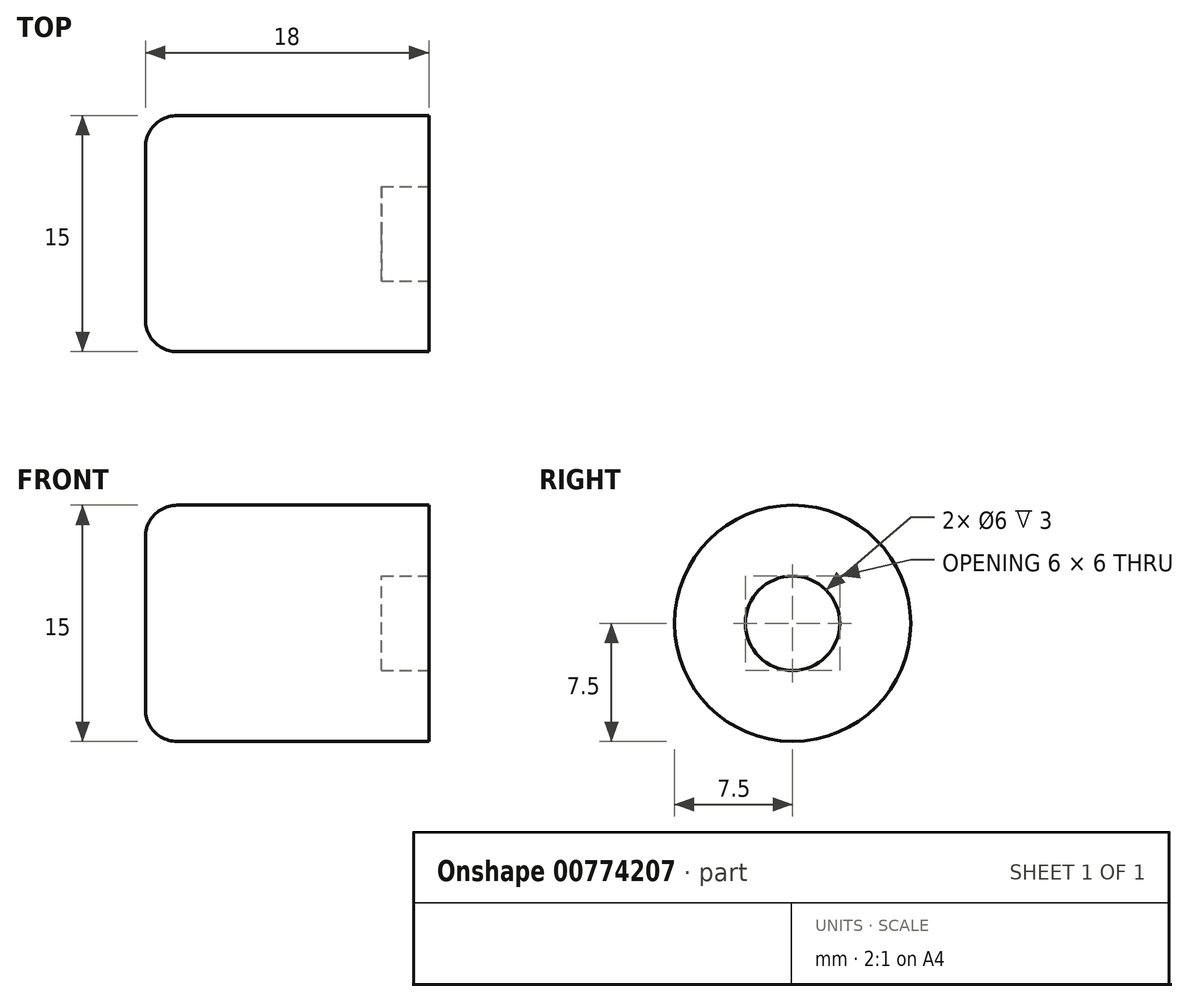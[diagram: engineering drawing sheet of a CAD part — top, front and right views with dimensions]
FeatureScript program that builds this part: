
annotation { "Feature Type Name" : "Feature", "Feature Type Description" : "" }
export const myFeature = defineFeature(function(context is Context, id is Id, definition is map)
    precondition{}
    {
        {
            var Q0;
            Q0=qCreatedBy(makeId("Front.planeOp"),FACE);
            var sketch = newSketch(context, id + "F0", { "sketchPlane" : qUnion([Q0])});
            skLineSegment(sketch, "E0.bottom", {"start": v(-15, 10) * mm, "end": v(15, 10) * mm});
            skLineSegment(sketch, "E0.top", {"start": v(-15, -10) * mm, "end": v(15, -10) * mm});
            skLineSegment(sketch, "E0.left", {"start": v(-15, 10) * mm, "end": v(-15, -10) * mm});
            skLineSegment(sketch, "E0.right", {"start": v(15, 10) * mm, "end": v(15, -10) * mm});
            skLineSegment(sketch, "E1", {"start": v(-17, 12) * mm, "end": v(-17, -12) * mm});
            skLineSegment(sketch, "E2", {"start": v(-17, -12) * mm, "end": v(17, -12) * mm});
            skLineSegment(sketch, "E3", {"start": v(17, -12) * mm, "end": v(17, 12) * mm});
            skLineSegment(sketch, "E4", {"start": v(17, 12) * mm, "end": v(-17, 12) * mm});
            skSolve(sketch);
        }
        {
            var Q0;
            Q0=makeQuery(id+"F0.imprint","IMPRINT",FACE,{"disambiguationData":[TD([[makeQuery(id+"F0.imprint","IMPRINT",EDGE,{"derivedFrom":sQuery(id+"F0.wireOp",EDGE,"E0.bottom")}),1.0]])]});
            extrude(context, id + "F1", {"entities" : qUnion([Q0]), "depth" : 20 * mm, "offsetDistance" : 25 * mm});
        }
        {
            var Q0;
            Q0=makeQuery(id+"F1.opExtrude","SWEPT_FACE",FACE,{"disambiguationData":[OSD([sQuery(id+"F0.wireOp",EDGE,"E4")])]});
            var sketch = newSketch(context, id + "F2", { "sketchPlane" : qUnion([Q0])});
            skCircle(sketch, "E5", {"center": v(6, -10) * mm, "radius": 6.5 * mm});
            skSolve(sketch);
        }
        {
            var Q0;
            Q0 = qSketchRegion(id + "F2", true);
            extrude(context, id + "F3", {"entities" : qUnion([Q0]), "operationType" : NewBodyOperationType.REMOVE, "oppositeDirection" : true, "depth" : 11.7 * mm, "offsetDistance" : 25 * mm});
        }
        {
            var Q0;
            Q0=makeQuery(id+"F1.opExtrude","SWEPT_FACE",FACE,{"disambiguationData":[OSD([sQuery(id+"F0.wireOp",EDGE,"E2")])]});
            var sketch = newSketch(context, id + "F4", { "sketchPlane" : qUnion([Q0])});
            skCircle(sketch, "E6", {"center": v(-5, 10) * mm, "radius": 7.5 * mm});
            skSolve(sketch);
        }
        {
            var Q0;
            Q0 = qSketchRegion(id + "F4", true);
            extrude(context, id + "F5", {"entities" : qUnion([Q0]), "operationType" : NewBodyOperationType.REMOVE, "oppositeDirection" : true, "depth" : 8.3 * mm, "offsetDistance" : 25 * mm});
        }
        {
            var Q0;
            Q0=makeQuery(id+"F1.opExtrude","SWEPT_FACE",FACE,{"disambiguationData":[OSD([sQuery(id+"F0.wireOp",EDGE,"E1")])]});
            var sketch = newSketch(context, id + "F6", { "sketchPlane" : qUnion([Q0])});
            skCircle(sketch, "E7", {"center": v(10, 0) * mm, "radius": 7.5 * mm});
            skSolve(sketch);
        }
        {
            var Q0;
            Q0 = qSketchRegion(id + "F6", true);
            extrude(context, id + "F7", {"entities" : qUnion([Q0]), "operationType" : NewBodyOperationType.ADD, "depth" : 18 * mm, "offsetDistance" : 25 * mm});
        }
        {
            var Q0;
            Q0=makeQuery(id+"F1.opExtrude","SWEPT_EDGE",EDGE,{"disambiguationData":[OSD([sQuery(id+"F0.wireOp",EDGE,"E1"),sQuery(id+"F0.wireOp",EDGE,"E4")])]});
            var Q1;
            Q1=makeQuery(id+"F1.opExtrude","SWEPT_EDGE",EDGE,{"disambiguationData":[OSD([sQuery(id+"F0.wireOp",EDGE,"E1"),sQuery(id+"F0.wireOp",EDGE,"E2")])]});
            var Q2;
            Q2=makeQuery(id+"F7.opExtrude","CAP_EDGE",EDGE,{"disambiguationData":[OSD([sQuery(id+"F6.wireOp",EDGE,"E7")])],"isStart":false});
            fillet(context, id + "F8", {"entities" : qUnion([Q0, Q1, Q2]), "radius" : 2 * mm, "tangentPropagation" : true, "allowEdgeOverflow" : false});
        }
        {
            var Q0;
            Q0=makeQuery(id+"F3.boolean.opBoolean","INTERSECT",EDGE,{"derivedFrom":[makeQuery(id+"F1.opExtrude","SWEPT_FACE",FACE,{"disambiguationData":[OSD([sQuery(id+"F0.wireOp",EDGE,"E0.bottom")])]}),makeQuery(id+"F3.opExtrude","SWEPT_FACE",FACE,{"disambiguationData":[OSD([sQuery(id+"F2.wireOp",EDGE,"E5")])]})]});
            var Q1;
            Q1=makeQuery(id+"F3.boolean.opBoolean","COPY",EDGE,{"derivedFrom":makeQuery(id+"F3.opExtrude","CAP_EDGE",EDGE,{"disambiguationData":[OSD([sQuery(id+"F2.wireOp",EDGE,"E5")])],"isStart":true})});
            var Q2;
            Q2=makeQuery(id+"F5.boolean.opBoolean","INTERSECT",EDGE,{"derivedFrom":[makeQuery(id+"F1.opExtrude","SWEPT_FACE",FACE,{"disambiguationData":[OSD([sQuery(id+"F0.wireOp",EDGE,"E0.top")])]}),makeQuery(id+"F5.opExtrude","SWEPT_FACE",FACE,{"disambiguationData":[OSD([sQuery(id+"F4.wireOp",EDGE,"E6")])]})]});
            var Q3;
            Q3=makeQuery(id+"F5.boolean.opBoolean","COPY",EDGE,{"derivedFrom":makeQuery(id+"F5.opExtrude","CAP_EDGE",EDGE,{"disambiguationData":[OSD([sQuery(id+"F4.wireOp",EDGE,"E6")])],"isStart":true})});
            fillet(context, id + "F9", {"entities" : qUnion([Q0, Q1, Q2, Q3]), "radius" : 1 * mm, "tangentPropagation" : true, "allowEdgeOverflow" : false});
        }
        {
            var Q0;
            Q0=makeQuery(id+"F1.opExtrude","CAP_FACE",FACE,{"disambiguationData":[OSD([sQuery(id+"F0.wireOp",EDGE,"E0.bottom"),sQuery(id+"F0.wireOp",EDGE,"E0.top"),sQuery(id+"F0.wireOp",EDGE,"E0.left"),sQuery(id+"F0.wireOp",EDGE,"E0.right"),sQuery(id+"F0.wireOp",EDGE,"E1"),sQuery(id+"F0.wireOp",EDGE,"E2"),sQuery(id+"F0.wireOp",EDGE,"E3"),sQuery(id+"F0.wireOp",EDGE,"E4")])],"isStart":false});
            var sketch = newSketch(context, id + "F10", { "sketchPlane" : qUnion([Q0])});
            skLineSegment(sketch, "E8.bottom", {"start": v(17, -10) * mm, "end": v(15, -10) * mm});
            skLineSegment(sketch, "E8.top", {"start": v(17, 10) * mm, "end": v(15, 10) * mm});
            skLineSegment(sketch, "E8.left", {"start": v(17, -10) * mm, "end": v(17, 10) * mm});
            skLineSegment(sketch, "E8.right", {"start": v(15, -10) * mm, "end": v(15, 10) * mm});
            skSolve(sketch);
        }
        {
            var Q0;
            Q0 = qSketchRegion(id + "F10", true);
            extrude(context, id + "F11", {"entities" : qUnion([Q0]), "operationType" : NewBodyOperationType.REMOVE, "oppositeDirection" : true, "depth" : 25 * mm, "offsetDistance" : 25 * mm});
        }
        {
            var Q0;
            Q0=qCreatedBy(makeId("Right.planeOp"),FACE);
            var sketch = newSketch(context, id + "F12", { "sketchPlane" : qUnion([Q0])});
            skLineSegment(sketch, "E9.bottom", {"start": v(-20, 12) * mm, "end": v(0, 12) * mm, "construction": true});
            skLineSegment(sketch, "E9.top", {"start": v(-20, -12) * mm, "end": v(0, -12) * mm, "construction": true});
            skLineSegment(sketch, "E9.left", {"start": v(-20, 12) * mm, "end": v(-20, -12) * mm, "construction": true});
            skLineSegment(sketch, "E9.right", {"start": v(0, 12) * mm, "end": v(0, -12) * mm, "construction": true});
            skArc(sketch, "E10", {"start": v(-20, 12) * mm, "mid": v(-21, 11) * mm, "end": v(-20, 10) * mm});
            skArc(sketch, "E11", {"start": v(-20, -10) * mm, "mid": v(-21, -11) * mm, "end": v(-20, -12) * mm});
            skArc(sketch, "E12", {"start": v(0, -12) * mm, "mid": v(1, -11) * mm, "end": v(0, -10) * mm});
            skArc(sketch, "E13", {"start": v(0, 10) * mm, "mid": v(1, 11) * mm, "end": v(0, 12) * mm});
            skLineSegment(sketch, "E14", {"start": v(-20, 10) * mm, "end": v(-20, 12) * mm});
            skLineSegment(sketch, "E15", {"start": v(0, 12) * mm, "end": v(0, 10) * mm});
            skLineSegment(sketch, "E16", {"start": v(0, -10) * mm, "end": v(0, -12) * mm});
            skLineSegment(sketch, "E17", {"start": v(-20, -10) * mm, "end": v(-20, -12) * mm});
            skArc(sketch, "E18", {"start": v(-20, -12) * mm, "mid": v(-19.5, -12.5) * mm, "end": v(-19, -12) * mm});
            skArc(sketch, "E19", {"start": v(-1, -12) * mm, "mid": v(-0.5, -12.5) * mm, "end": v(0, -12) * mm});
            skLineSegment(sketch, "E20", {"start": v(-19, -12) * mm, "end": v(-20, -12) * mm});
            skLineSegment(sketch, "E21", {"start": v(-1, -12) * mm, "end": v(0, -12) * mm});
            skArc(sketch, "E22", {"start": v(-20, 10) * mm, "mid": v(-19.5, 9.5) * mm, "end": v(-19, 10) * mm});
            skArc(sketch, "E23", {"start": v(-1, 10) * mm, "mid": v(-0.5, 9.5) * mm, "end": v(0, 10) * mm});
            skLineSegment(sketch, "E24", {"start": v(-19, 10) * mm, "end": v(-20, 10) * mm});
            skLineSegment(sketch, "E25", {"start": v(0, 10) * mm, "end": v(-1, 10) * mm});
            skSolve(sketch);
        }
        {
            var Q0;
            Q0 = qSketchRegion(id + "F12", true);
            extrude(context, id + "F13", {"entities" : qUnion([Q0]), "operationType" : NewBodyOperationType.ADD, "endBound" : BoundingType.SYMMETRIC, "depth" : 30 * mm, "offsetDistance" : 25 * mm});
        }
        {
            var Q0;
            Q0=makeQuery(id+"F13.opExtrude","CAP_EDGE",EDGE,{"disambiguationData":[OSD([sQuery(id+"F12.wireOp",EDGE,"E10")])],"isStart":false});
            var Q1;
            Q1=makeQuery(id+"F13.opExtrude","CAP_EDGE",EDGE,{"disambiguationData":[OSD([sQuery(id+"F12.wireOp",EDGE,"E10")])],"isStart":true});
            var Q2;
            Q2=makeQuery(id+"F13.opExtrude","CAP_EDGE",EDGE,{"disambiguationData":[OSD([sQuery(id+"F12.wireOp",EDGE,"E11")])],"isStart":true});
            var Q3;
            Q3=makeQuery(id+"F13.opExtrude","CAP_EDGE",EDGE,{"disambiguationData":[OSD([sQuery(id+"F12.wireOp",EDGE,"E11")])],"isStart":false});
            var Q4;
            Q4=makeQuery(id+"F13.opExtrude","CAP_EDGE",EDGE,{"disambiguationData":[OSD([sQuery(id+"F12.wireOp",EDGE,"E13")])],"isStart":true});
            var Q5;
            Q5=makeQuery(id+"F13.opExtrude","CAP_EDGE",EDGE,{"disambiguationData":[OSD([sQuery(id+"F12.wireOp",EDGE,"E12")])],"isStart":true});
            var Q6;
            Q6=makeQuery(id+"F13.opExtrude","CAP_EDGE",EDGE,{"disambiguationData":[OSD([sQuery(id+"F12.wireOp",EDGE,"E12")])],"isStart":false});
            var Q7;
            Q7=makeQuery(id+"F13.opExtrude","CAP_EDGE",EDGE,{"disambiguationData":[OSD([sQuery(id+"F12.wireOp",EDGE,"E13")])],"isStart":false});
            fillet(context, id + "F14", {"entities" : qUnion([Q0, Q1, Q2, Q3, Q4, Q5, Q6, Q7]), "radius" : 1 * mm, "tangentPropagation" : true, "allowEdgeOverflow" : false});
        }
        {
            var Q0;
            Q0=makeQuery(id+"F13.opExtrude","CAP_EDGE",EDGE,{"disambiguationData":[OSD([sQuery(id+"F12.wireOp",EDGE,"E19")])],"isStart":false});
            var Q1;
            Q1=makeQuery(id+"F13.opExtrude","CAP_EDGE",EDGE,{"disambiguationData":[OSD([sQuery(id+"F12.wireOp",EDGE,"E18")])],"isStart":false});
            var Q2;
            Q2=makeQuery(id+"F13.opExtrude","CAP_EDGE",EDGE,{"disambiguationData":[OSD([sQuery(id+"F12.wireOp",EDGE,"E18")])],"isStart":true});
            var Q3;
            Q3=makeQuery(id+"F13.opExtrude","CAP_EDGE",EDGE,{"disambiguationData":[OSD([sQuery(id+"F12.wireOp",EDGE,"E19")])],"isStart":true});
            var Q4;
            Q4=makeQuery(id+"F13.opExtrude","CAP_EDGE",EDGE,{"disambiguationData":[OSD([sQuery(id+"F12.wireOp",EDGE,"E22")])],"isStart":false});
            var Q5;
            Q5=makeQuery(id+"F13.opExtrude","CAP_EDGE",EDGE,{"disambiguationData":[OSD([sQuery(id+"F12.wireOp",EDGE,"E23")])],"isStart":false});
            fillet(context, id + "F15", {"entities" : qUnion([Q0, Q1, Q2, Q3, Q4, Q5]), "radius" : 0.5 * mm, "tangentPropagation" : true, "allowEdgeOverflow" : false});
        }
        {
            var Q0;
            Q0=makeQuery(id+"F1.opExtrude","SWEPT_FACE",FACE,{"disambiguationData":[OSD([sQuery(id+"F0.wireOp",EDGE,"E0.left")])]});
            var sketch = newSketch(context, id + "F16", { "sketchPlane" : qUnion([Q0])});
            skCircle(sketch, "E26", {"center": v(-10, 0) * mm, "radius": 3 * mm});
            skSolve(sketch);
        }
        {
            var Q0;
            Q0 = qSketchRegion(id + "F16", true);
            extrude(context, id + "F17", {"entities" : qUnion([Q0]), "operationType" : NewBodyOperationType.REMOVE, "oppositeDirection" : true, "depth" : 5 * mm, "offsetDistance" : 25 * mm});
        }
        {
            var Q0;
            Q0=makeQuery(id+"F1.opExtrude","SWEPT_FACE",FACE,{"disambiguationData":[OSD([sQuery(id+"F0.wireOp",EDGE,"E1")])]});
            var sketch = newSketch(context, id + "F18", { "sketchPlane" : qUnion([Q0])});
            skLineSegment(sketch, "E27.bottom", {"start": v(-11.92, 13.69) * mm, "end": v(28.43, 13.69) * mm});
            skLineSegment(sketch, "E27.top", {"start": v(-11.92, -21.95) * mm, "end": v(28.43, -21.95) * mm});
            skLineSegment(sketch, "E27.left", {"start": v(-11.92, 13.69) * mm, "end": v(-11.92, -21.95) * mm});
            skLineSegment(sketch, "E27.right", {"start": v(28.43, 13.69) * mm, "end": v(28.43, -21.95) * mm});
            skSolve(sketch);
        }
        {
            var Q0;
            Q0=makeQuery(id+"F1.opExtrude","SWEPT_BODY",BODY,{"disambiguationData":[OSD([sQuery(id+"F0.wireOp",EDGE,"E0.bottom"),sQuery(id+"F0.wireOp",EDGE,"E0.top"),sQuery(id+"F0.wireOp",EDGE,"E0.left"),sQuery(id+"F0.wireOp",EDGE,"E0.right"),sQuery(id+"F0.wireOp",EDGE,"E1"),sQuery(id+"F0.wireOp",EDGE,"E2"),sQuery(id+"F0.wireOp",EDGE,"E3"),sQuery(id+"F0.wireOp",EDGE,"E4")])]});
            transform(context, id + "F19", {"entities" : qUnion([Q0]), "transformType" : TransformType.TRANSLATION_3D, "dx" : 0 * mm, "dy" : 0 * mm, "dz" : 0 * mm, "makeCopy" : true});
        }
        {
            var Q0;
            Q0 = qSketchRegion(id + "F18", true);
            extrude(context, id + "F20", {"entities" : qUnion([Q0]), "operationType" : NewBodyOperationType.REMOVE, "oppositeDirection" : true, "depth" : 56.6 * mm, "offsetDistance" : 25 * mm});
        }
        {
            var Q0;
            Q0 = qSketchRegion(id + "F18", true);
            extrude(context, id + "F21", {"entities" : qUnion([Q0]), "operationType" : NewBodyOperationType.REMOVE, "oppositeDirection" : true, "depth" : 74.7 * mm, "offsetDistance" : 25 * mm});
        }
    });
